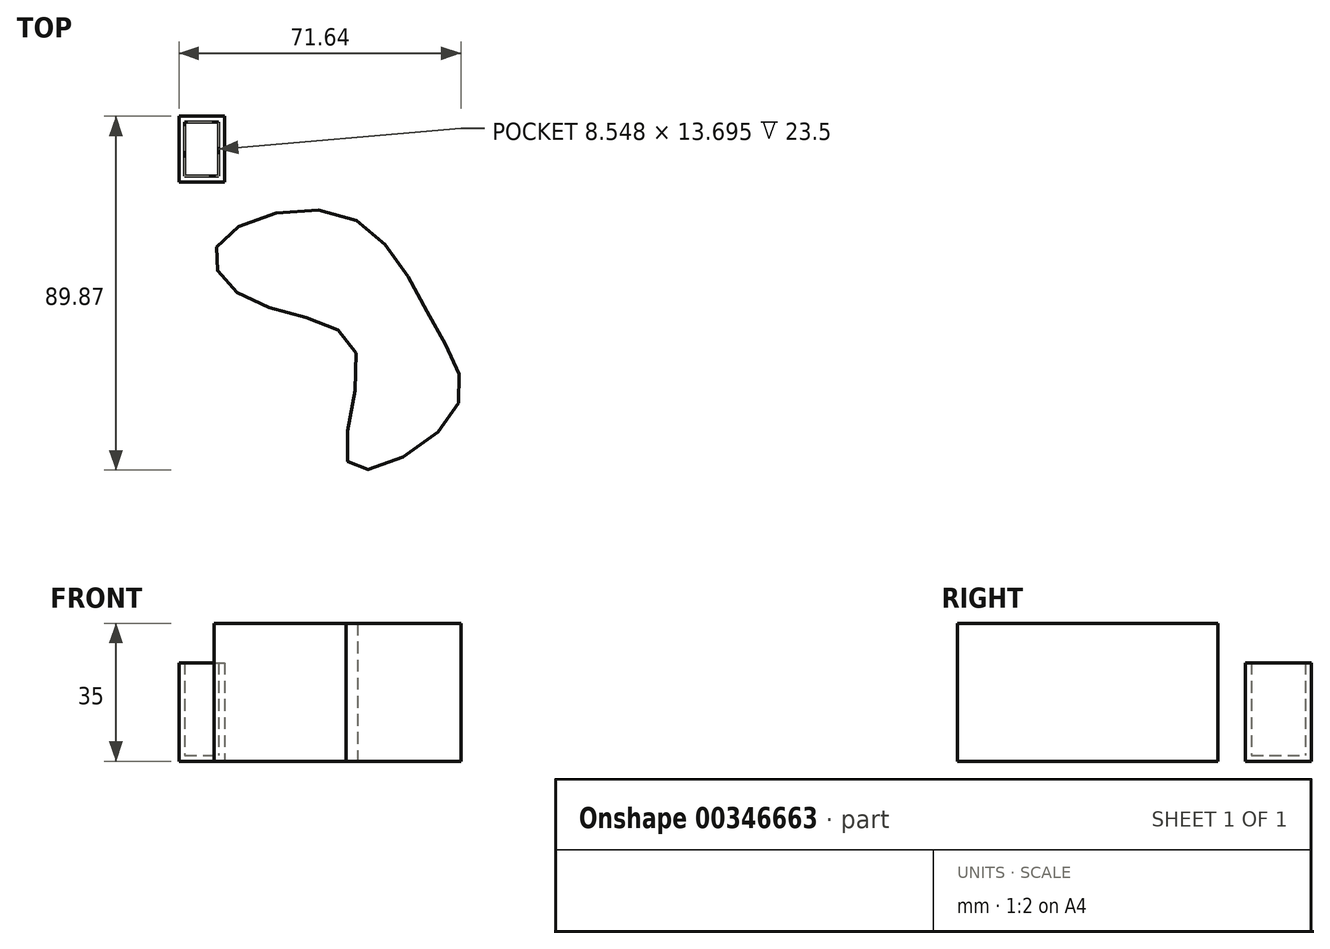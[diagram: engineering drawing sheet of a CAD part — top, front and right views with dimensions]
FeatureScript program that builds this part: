
annotation { "Feature Type Name" : "Feature", "Feature Type Description" : "" }
export const myFeature = defineFeature(function(context is Context, id is Id, definition is map)
    precondition{}
    {
        {
            var Q0;
            Q0=qCreatedBy(makeId("Top.planeOp"),FACE);
            var sketch = newSketch(context, id + "F0", { "sketchPlane" : qUnion([Q0])});
            skFitSpline(sketch, "E0", {"points": [v(-48.3, 29.48) * mm, v(-16.68, 37.82) * mm, v(6.6, 10.47) * mm, v(12.03, -12.6) * mm, v(-14.16, -26.19) * mm, v(-13.19, 3.5) * mm, v(-38.8, 15.52) * mm, v(-48.3, 29.48) * mm]});
            skSolve(sketch);
        }
        {
            var Q0;
            Q0=makeQuery(id+"F0.imprint","IMPRINT",FACE,{"disambiguationData":[TD([[makeQuery(id+"F0.imprint","IMPRINT",EDGE,{"derivedFrom":sQuery(id+"F0.wireOp",EDGE,"E0")}),-1.0]])]});
            extrude(context, id + "F1", {"entities" : qUnion([Q0]), "depth" : 35 * mm});
        }
        {
            var Q0;
            Q0=qCreatedBy(makeId("Top.planeOp"),FACE);
            var sketch = newSketch(context, id + "F2", { "sketchPlane" : qUnion([Q0])});
            skLineSegment(sketch, "E1.bottom", {"start": v(-57.9, 46.02) * mm, "end": v(-46.34, 46.02) * mm});
            skLineSegment(sketch, "E1.top", {"start": v(-57.9, 62.72) * mm, "end": v(-46.34, 62.72) * mm});
            skLineSegment(sketch, "E1.left", {"start": v(-57.9, 46.02) * mm, "end": v(-57.9, 62.72) * mm});
            skLineSegment(sketch, "E1.right", {"start": v(-46.34, 46.02) * mm, "end": v(-46.34, 62.72) * mm});
            skSolve(sketch);
        }
        {
            var Q0;
            Q0=makeQuery(id+"F2.imprint","IMPRINT",FACE,{"disambiguationData":[TD([[makeQuery(id+"F2.imprint","IMPRINT",EDGE,{"derivedFrom":sQuery(id+"F2.wireOp",EDGE,"E1.bottom")}),1.0]])]});
            extrude(context, id + "F3", {"entities" : qUnion([Q0]), "depth" : 25 * mm});
        }
        {
            var Q0;
            Q0=makeQuery(id+"F3.opExtrude","CAP_FACE",FACE,{"disambiguationData":[OSD([sQuery(id+"F2.wireOp",EDGE,"E1.bottom"),sQuery(id+"F2.wireOp",EDGE,"E1.top"),sQuery(id+"F2.wireOp",EDGE,"E1.left"),sQuery(id+"F2.wireOp",EDGE,"E1.right")])],"isStart":false});
            shell(context, id + "F4", {"entities" : qUnion([Q0]), "thickness" : 1.5 * mm});
        }
    });
